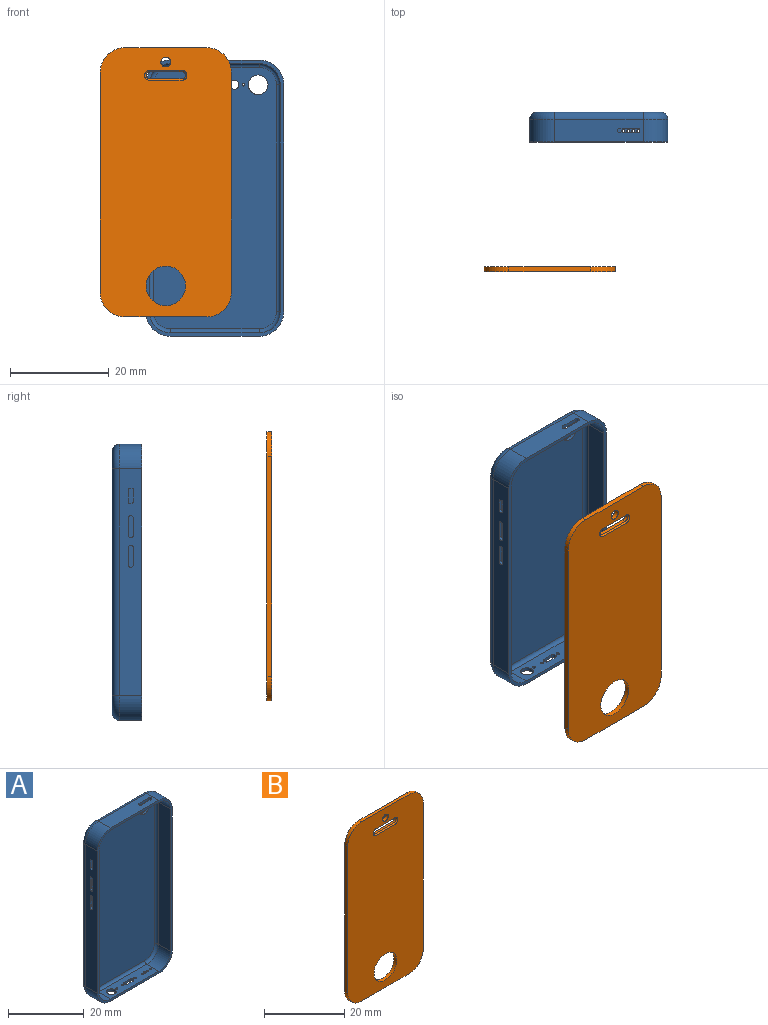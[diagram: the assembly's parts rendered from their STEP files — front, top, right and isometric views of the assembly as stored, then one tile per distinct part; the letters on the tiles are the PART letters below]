
ASSEMBLY  parts=2 mates=1
PART A: 70 faces, bbox 28.8x6x56.8 mm
  f0: plane 18x4.5mm, normal (0,0,1), area 76.7mm2, adj f2,f7,f10,f14,f63,f64,f65,f66
  f1: plane 18x4.5mm, normal (0,0,-1), area 76.7mm2, adj f2,f23,f26,f30,f63,f64,f65,f66
  f2: plane 56x28mm, normal (0,-1,0), area 110.1mm2, adj f0,f1,f3,f4,f5,f7,f8,f9
  f3: plane 46x4.5mm, normal (-1,0,0), area 195.5mm2, adj f2,f7,f8,f11,f47,f48,f49,f50
  f4: plane 18x4.5mm, normal (0,0,-1), area 70.6mm2, adj f2,f8,f9,f15,f35,f36,f37,f38
  f5: plane 46x4.5mm, normal (1,0,0), area 207mm2, adj f2,f9,f10,f18
  f6: plane 53x25mm, normal (0,1,0), area 1299.2mm2, adj f11,f12,f13,f14,f15,f16,f17,f18
  f7: cylinder r=5mm len=5mm, axis (0,-1,0), area 35.3mm2, adj f0,f2,f3,f12
  f8: cylinder r=5mm len=5mm, axis (0,1,0), area 35.3mm2, adj f2,f3,f4,f13
  f9: cylinder r=5mm len=5mm, axis (0,-1,0), area 35.3mm2, adj f2,f4,f5,f17
  f10: cylinder r=5mm len=5mm, axis (0,1,0), area 35.3mm2, adj f0,f2,f5,f16
  f11: cylinder r=1.5mm len=46mm, axis (0,0,-1), area 108.4mm2, adj f3,f6,f12,f13
  f12: torus R=3.5mm, axis (0,-1,0), area 16.5mm2, adj f6,f7,f11,f14
  f13: torus R=3.5mm, axis (0,-1,0), area 16.5mm2, adj f6,f8,f11,f15
  f14: cylinder r=1.5mm len=18mm, axis (-1,0,0), area 42.4mm2, adj f0,f6,f12,f16
  f15: cylinder r=1.5mm len=18mm, axis (1,0,0), area 42.4mm2, adj f4,f6,f13,f17
  f16: torus R=3.5mm, axis (0,-1,0), area 16.5mm2, adj f6,f10,f14,f18
  f17: torus R=3.5mm, axis (0,-1,0), area 16.5mm2, adj f6,f9,f15,f18
  f18: cylinder r=1.5mm len=46mm, axis (0,0,1), area 108.4mm2, adj f5,f6,f16,f17
  f19: plane 46x4.5mm, normal (1,0,0), area 195.5mm2, adj f2,f23,f24,f27,f47,f48,f49,f50
  f20: plane 18x4.5mm, normal (0,0,1), area 70.6mm2, adj f2,f24,f25,f31,f35,f36,f37,f38
  f21: plane 46x4.5mm, normal (-1,0,0), area 207mm2, adj f2,f25,f26,f34
  f22: plane 53x25mm, normal (0,-1,0), area 1299.2mm2, adj f27,f28,f29,f30,f31,f32,f33,f34
  f23: cylinder r=4.3mm len=4.5mm, axis (0,-1,0), area 30.4mm2, adj f1,f2,f19,f28
  f24: cylinder r=4.3mm len=4.5mm, axis (0,1,0), area 30.4mm2, adj f2,f19,f20,f29
  f25: cylinder r=4.3mm len=4.5mm, axis (0,-1,0), area 30.4mm2, adj f2,f20,f21,f33
  f26: cylinder r=4.3mm len=4.5mm, axis (0,1,0), area 30.4mm2, adj f1,f2,f21,f32
  f27: cylinder r=0.8mm len=46mm, axis (0,0,-1), area 57.8mm2, adj f19,f22,f28,f29
  f28: torus R=3.5mm, axis (0,-1,0), area 7.9mm2, adj f22,f23,f27,f30
  f29: torus R=3.5mm, axis (0,-1,0), area 7.9mm2, adj f22,f24,f27,f31
  f30: cylinder r=0.8mm len=18mm, axis (-1,0,0), area 22.6mm2, adj f1,f22,f28,f32
  f31: cylinder r=0.8mm len=18mm, axis (1,0,0), area 22.6mm2, adj f20,f22,f29,f33
  f32: torus R=3.5mm, axis (0,-1,0), area 7.9mm2, adj f22,f26,f30,f34
  f33: torus R=3.5mm, axis (0,-1,0), area 7.9mm2, adj f22,f25,f31,f34
  f34: cylinder r=0.8mm len=46mm, axis (0,0,1), area 57.8mm2, adj f21,f22,f32,f33
  f35: cylinder r=0.6mm len=1.2mm, axis (0,0,-1), area 1.3mm2, adj f4,f20,f36,f37
  f36: plane 2x0.7mm, normal (0,1,0), area 1.4mm2, adj f4,f20,f35,f38
  f37: plane 2x0.7mm, normal (0,-1,0), area 1.4mm2, adj f4,f20,f35,f38
  f38: cylinder r=0.6mm len=1.2mm, axis (0,0,-1), area 1.3mm2, adj f4,f20,f36,f37
  f39: cylinder r=0.3mm len=0.7mm, axis (0,0,-1), area 1.3mm2, adj f4,f20
  f40: cylinder r=0.3mm len=0.7mm, axis (0,0,-1), area 1.3mm2, adj f4,f20
  f41: cylinder r=0.3mm len=0.7mm, axis (0,0,-1), area 1.3mm2, adj f4,f20
  f42: cylinder r=0.3mm len=0.7mm, axis (0,0,-1), area 1.3mm2, adj f4,f20
  f43: cylinder r=1.25mm len=2.5mm, axis (0,0,-1), area 5.5mm2, adj f4,f20
  f44: cylinder r=0.3mm len=0.7mm, axis (0,0,-1), area 1.3mm2, adj f4,f20
  f45: cylinder r=0.3mm len=0.7mm, axis (0,0,-1), area 1.3mm2, adj f4,f20
  f46: cylinder r=0.3mm len=0.7mm, axis (0,0,-1), area 1.3mm2, adj f4,f20
  f47: cylinder r=0.2mm len=0.7mm, axis (-1,0,0), area 0.2mm2, adj f3,f19,f48,f52
  f48: plane 2.6x0.7mm, normal (0,-1,0), area 1.8mm2, adj f3,f19,f47,f49
  f49: cylinder r=0.2mm len=0.7mm, axis (-1,0,0), area 0.2mm2, adj f3,f19,f48,f50
  f50: plane 0.7x0.6mm, normal (0,0,1), area 0.4mm2, adj f3,f19,f49,f51
  f51: cylinder r=0.2mm len=0.7mm, axis (-1,0,0), area 0.2mm2, adj f3,f19,f50,f53
  f52: plane 0.7x0.6mm, normal (0,0,-1), area 0.4mm2, adj f3,f19,f47,f54
  f53: plane 2.6x0.7mm, normal (0,1,0), area 1.8mm2, adj f3,f19,f51,f54
  f54: cylinder r=0.2mm len=0.7mm, axis (-1,0,0), area 0.2mm2, adj f3,f19,f52,f53
  f55: cylinder r=0.5mm len=1mm, axis (-1,0,0), area 1.1mm2, adj f3,f19,f56,f57
  f56: plane 3.5x0.7mm, normal (0,1,0), area 2.4mm2, adj f3,f19,f55,f58
  f57: plane 3.5x0.7mm, normal (0,-1,0), area 2.4mm2, adj f3,f19,f55,f58
  f58: cylinder r=0.5mm len=1mm, axis (-1,0,0), area 1.1mm2, adj f3,f19,f56,f57
  f59: cylinder r=0.5mm len=1mm, axis (-1,0,0), area 1.1mm2, adj f3,f19,f60,f62
  f60: plane 3.5x0.7mm, normal (0,-1,0), area 2.4mm2, adj f3,f19,f59,f61
  f61: cylinder r=0.5mm len=1mm, axis (-1,0,0), area 1.1mm2, adj f3,f19,f60,f62
  f62: plane 3.5x0.7mm, normal (0,1,0), area 2.4mm2, adj f3,f19,f59,f61
  f63: plane 3.5x0.7mm, normal (0,-1,0), area 2.4mm2, adj f0,f1,f64,f66
  f64: cylinder r=0.5mm len=1mm, axis (0,0,1), area 1.1mm2, adj f0,f1,f63,f65
  f65: plane 3.5x0.7mm, normal (0,1,0), area 2.4mm2, adj f0,f1,f64,f66
  f66: cylinder r=0.5mm len=1mm, axis (0,0,1), area 1.1mm2, adj f0,f1,f63,f65
  f67: cylinder r=0.9mm len=1.8mm, axis (0,1,0), area 4mm2, adj f6,f22
  f68: cylinder r=0.25mm len=0.7mm, axis (0,1,0), area 1.1mm2, adj f6,f22
  f69: cylinder r=2mm len=4mm, axis (0,1,0), area 8.8mm2, adj f6,f22
PART B: 20 faces, bbox 26.6x1x54.6 mm
  f0: plane 16.6x1mm, normal (0,0,1), area 16.6mm2, adj f1,f13,f14,f15
  f1: cylinder r=5mm len=5mm, axis (0,1,0), area 7.9mm2, adj f0,f2,f14,f15
  f2: plane 44.6x1mm, normal (-1,0,0), area 44.6mm2, adj f1,f3,f14,f15
  f3: cylinder r=5mm len=5mm, axis (0,1,0), area 7.9mm2, adj f2,f4,f14,f15
  f4: plane 16.6x1mm, normal (0,0,-1), area 16.6mm2, adj f3,f5,f14,f15
  f5: cylinder r=5mm len=5mm, axis (0,1,0), area 7.9mm2, adj f4,f6,f14,f15
  f6: plane 44.6x1mm, normal (1,0,0), area 44.6mm2, adj f5,f13,f14,f15
  f7: cylinder r=0.7mm len=1.4mm, axis (0,1,0), area 1.5mm2, adj f8,f10,f15,f17
  f8: plane 6.6x0.7mm, normal (0,0,-1), area 4.6mm2, adj f7,f9,f15,f16
  f9: cylinder r=0.7mm len=1.4mm, axis (0,1,0), area 1.5mm2, adj f8,f10,f15,f18
  f10: plane 6.6x0.7mm, normal (0,0,1), area 4.6mm2, adj f7,f9,f15,f19
  f11: cylinder r=4mm len=8mm, axis (0,1,0), area 25.1mm2, adj f14,f15
  f12: cylinder r=1mm len=2mm, axis (0,1,0), area 6.3mm2, adj f14,f15
  f13: cylinder r=5mm len=5mm, axis (0,1,0), area 7.9mm2, adj f0,f6,f14,f15
  f14: plane 54.6x26.6mm, normal (0,-1,0), area 1361.2mm2, adj f0,f1,f2,f3,f4,f5,f6,f11
  f15: plane 54.6x26.6mm, normal (0,1,0), area 1366.7mm2, adj f0,f1,f2,f3,f4,f5,f6,f7
  f16: plane 6.6x0.3mm, normal (0,-0.71,-0.71), area 2.8mm2, adj f8,f14,f17,f18
  f17: cone r=0.7mm half-angle=45deg, axis (0,-1,0), area 1.1mm2, adj f7,f14,f16,f19
  f18: cone r=0.7mm half-angle=45deg, axis (0,-1,0), area 1.1mm2, adj f9,f14,f16,f19
  f19: plane 6.6x0.3mm, normal (0,-0.71,0.71), area 2.8mm2, adj f10,f14,f17,f18
PLACE A t=(-9.83,14.49,-1.28)mm fixed
PLACE B t=(-19.77,-16.86,1.94)mm
MATE parallel B.f15 <-> A.f22  axis (0,1,0) through (-19.77,-16.86,2.48)mm
